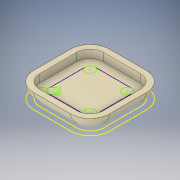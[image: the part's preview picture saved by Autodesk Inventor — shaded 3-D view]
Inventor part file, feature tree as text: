
AUTODESK INVENTOR PART (.ipt)
format: ipt  version: 2018 (Build 220112000, 112)  size: 882,176 bytes
history: native  units: in
note: dims shown in document units (in); Inventor stores cm internally (conversion verified against a paired STEP export)
features: other x14, extrude x6, sketch x4, plane x3, projected_geometry x3, delete_face x1
ambient origin geometry x8: Origin, YZ Plane, XZ Plane, XY Plane, X Axis, Y Axis, Z Axis, Center Point
bodies: Solid2 (feature_tree), Solid1 (feature_tree), Solid11 (feature_tree)
feature tree (31):
  other  "Remote Shell.ipt"
  other  "Initial Thicken"
  other  "Scoop Out"
  other  "Top Plane"
  plane  "Work Plane7"
  extrude  "Border Thicken Extrusion"  Depth=0.12in
  extrude  "Logo Cut"  Depth=0.01in TaperAngle=0.0deg
  other  "Registration Drill"
  plane  "Work Plane16"
  sketch  "Sketch28"  dims[d106=1.5in d108=0.0in d109=0.0in]
  extrude  "Extrusion14"  TaperAngle=0.0deg  [1 undecoded]
  extrude  "Extrusion15"  Depth=1.0in TaperAngle=0.0deg
  extrude  "Extrusion16"  Depth=0.1in TaperAngle=0.0deg
  plane  "Work Plane17"
  other  "Alignment Sketch"
  other  "Peg Sketch"
  extrude  "Extrusion17"  Depth=0.05in TaperAngle=0.0deg
  delete_face  "Delete Face1"
  other  "Bottom Solid::Remote Shell.ipt"
  other  "TaggingFeature1"
  other  "Srf1"
  other  "Srf2"
  sketch  "Sketch21"  dims[d0=0.3937in d3=0.12in d4=0.1in]
  other  "Top Solid::Remote Shell.ipt"
  sketch  "Sketch23"  dims[d91=0.0375in d92=0.02in d100=0.01in d101=0.0in]
  sketch  "Sketch29"  dims[d127=0.156in d128=1.0in d129=0.0in d130=0.1in d131=0.0in d132=0.05in d133=0.0in d134=0.252in d135=0.252in d136=0.252in d137=0.125in d138=0.125in d139=0.126in d140=0.126in d141=0.126in d142=0.126in d143=0.0in d144=0.075in d145=0.0in d146=0.252in d147=0.25in d148=0.1562in d149=0.1562in]
  projected_geometry  "Projected Loop5"
  projected_geometry  "Projected Loop13"
  projected_geometry  "Projected Loop14"
  other  "Srf1::Derived"
  other  "Srf2::Derived"
note: 1 required parameter value undecoded (feature->parameter linkage not recoverable at this tier; creation-order binding heuristic only, values carry confidence <= 0.55)
